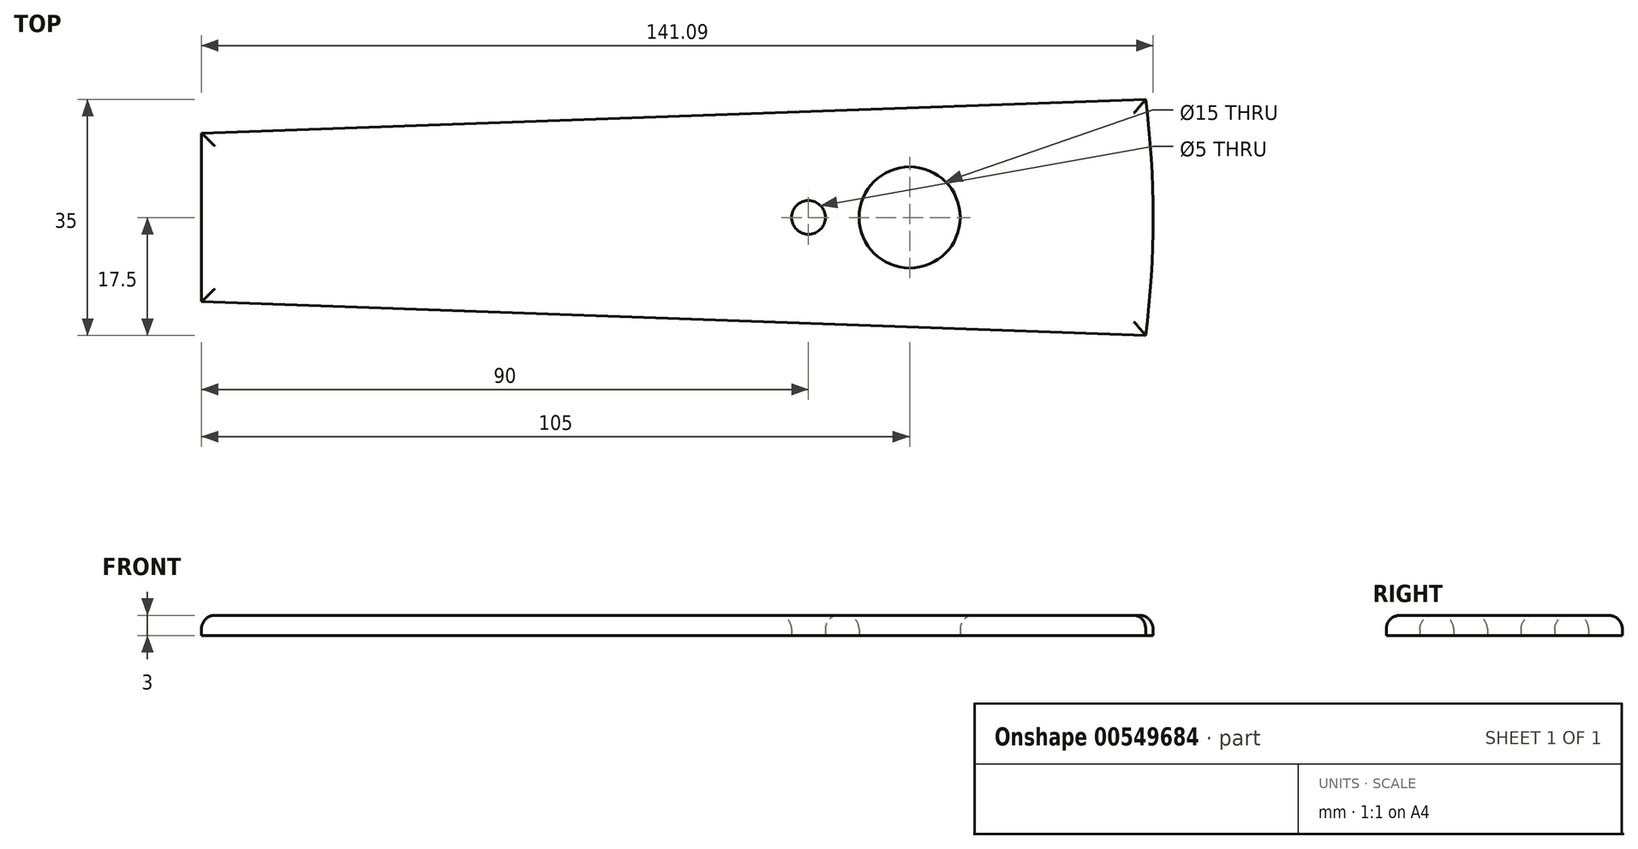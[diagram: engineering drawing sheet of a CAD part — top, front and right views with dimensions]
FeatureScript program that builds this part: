
annotation { "Feature Type Name" : "Feature", "Feature Type Description" : "" }
export const myFeature = defineFeature(function(context is Context, id is Id, definition is map)
    precondition{}
    {
        {
            var Q0;
            Q0=qCreatedBy(makeId("Top.planeOp"),FACE);
            var sketch = newSketch(context, id + "F0", { "sketchPlane" : qUnion([Q0])});
            skPoint(sketch, "E0", {"position": v(-70, 12.5) * mm});
            skPoint(sketch, "E1", {"position": v(-70, -12.5) * mm});
            skPoint(sketch, "E2", {"position": v(70, -17.5) * mm});
            skPoint(sketch, "E3", {"position": v(70, 17.5) * mm});
            skLineSegment(sketch, "E4", {"start": v(-70, 12.5) * mm, "end": v(-70, -12.5) * mm});
            skLineSegment(sketch, "E5", {"start": v(-70, -12.5) * mm, "end": v(70, -17.5) * mm});
            skLineSegment(sketch, "E6", {"start": v(-70, 12.5) * mm, "end": v(70, 17.5) * mm});
            skArc(sketch, "E7", {"start": v(70, -17.5) * mm, "mid": v(71.09, 0) * mm, "end": v(70, 17.5) * mm});
            skPoint(sketch, "E8", {"position": v(-70, -4.5) * mm});
            skPoint(sketch, "E9", {"position": v(-70, 4.5) * mm});
            skPoint(sketch, "E10", {"position": v(70.77, 9.5) * mm});
            skPoint(sketch, "E11", {"position": v(70.77, -9.5) * mm});
            skCircle(sketch, "E12", {"center": v(35, 0) * mm, "radius": 7.5 * mm});
            skCircle(sketch, "E13", {"center": v(20, 0) * mm, "radius": 2.5 * mm});
            skSolve(sketch);
        }
        {
            var Q0;
            Q0=makeQuery(id+"F0.imprint","IMPRINT",FACE,{"disambiguationData":[TD([[makeQuery(id+"F0.imprint","IMPRINT",EDGE,{"derivedFrom":sQuery(id+"F0.wireOp",EDGE,"E4")}),1.0]])]});
            extrude(context, id + "F1", {"entities" : qUnion([Q0]), "depth" : 3 * mm, "offsetDistance" : 25 * mm});
        }
        {
            var Q0;
            Q0=makeQuery(id+"F1.opExtrude","CAP_FACE",FACE,{"disambiguationData":[OSD([sQuery(id+"F0.wireOp",EDGE,"E4"),sQuery(id+"F0.wireOp",EDGE,"E5"),sQuery(id+"F0.wireOp",EDGE,"E6"),sQuery(id+"F0.wireOp",EDGE,"E7"),sQuery(id+"F0.wireOp",EDGE,"E12"),sQuery(id+"F0.wireOp",EDGE,"E13")])],"isStart":false});
            fillet(context, id + "F2", {"entities" : qUnion([Q0]), "radius" : 2 * mm, "tangentPropagation" : true, "allowEdgeOverflow" : false});
        }
    });
